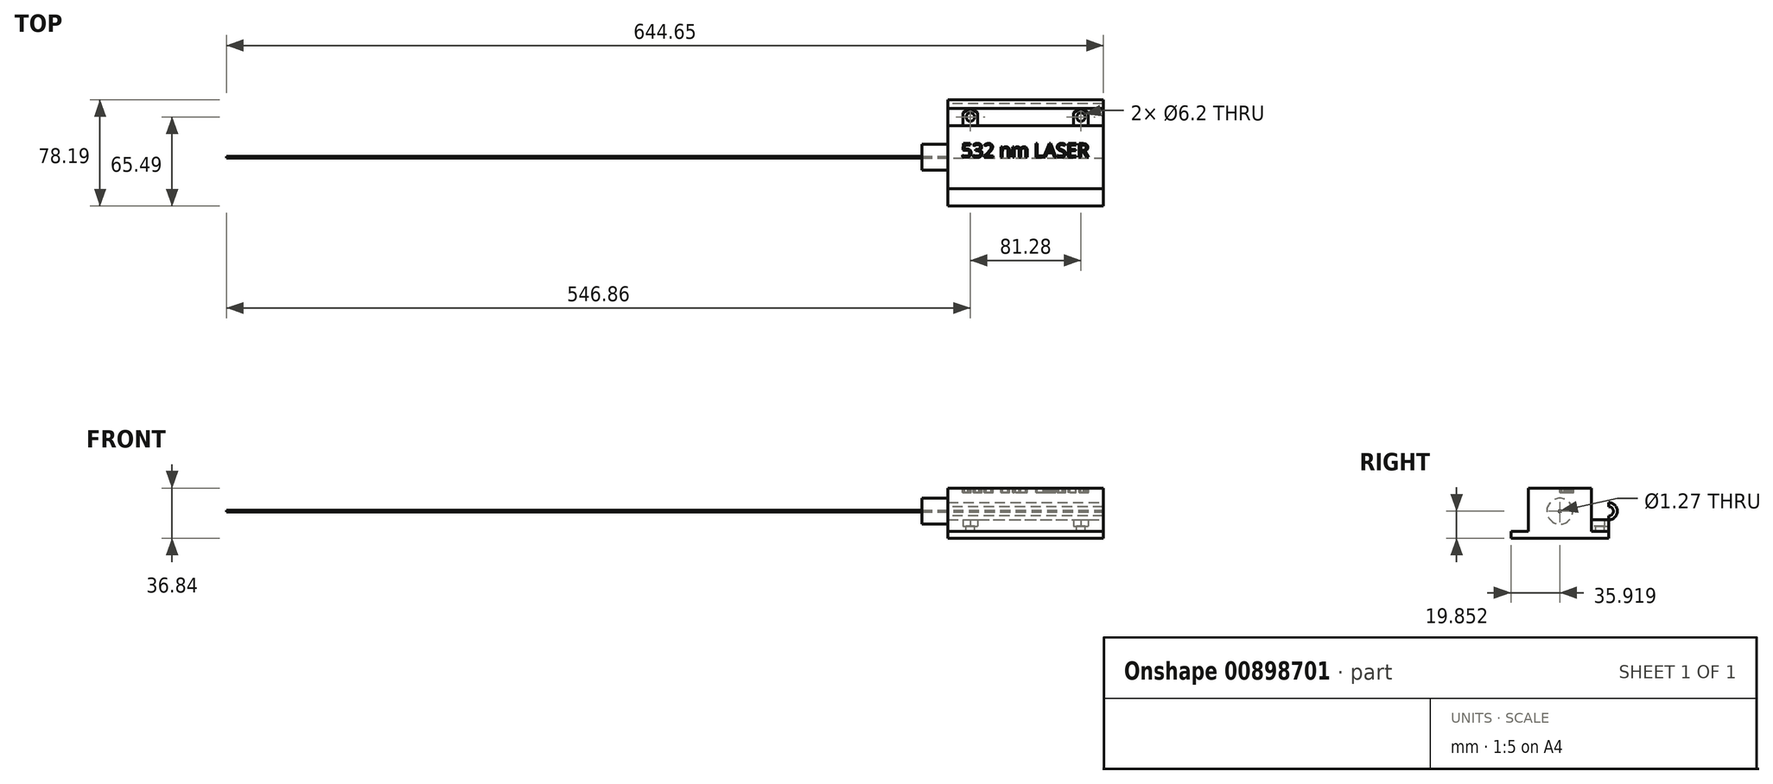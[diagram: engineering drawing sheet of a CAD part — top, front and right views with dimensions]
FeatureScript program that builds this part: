
annotation { "Feature Type Name" : "Feature", "Feature Type Description" : "" }
export const myFeature = defineFeature(function(context is Context, id is Id, definition is map)
    precondition{}
    {
        {
            var Q0;
            Q0=qCreatedBy(makeId("Top.planeOp"),FACE);
            var sketch = newSketch(context, id + "F0", { "sketchPlane" : qUnion([Q0])});
            skLineSegment(sketch, "E0.bottom", {"start": v(-57.15, 6.35) * mm, "end": v(57.15, 6.35) * mm});
            skLineSegment(sketch, "E0.top", {"start": v(-57.15, -6.35) * mm, "end": v(57.15, -6.35) * mm});
            skLineSegment(sketch, "E0.left", {"start": v(-57.15, 6.35) * mm, "end": v(-57.15, -6.35) * mm});
            skLineSegment(sketch, "E0.right", {"start": v(57.15, 6.35) * mm, "end": v(57.15, -6.35) * mm});
            skLineSegment(sketch, "E1", {"start": v(-57.15, 0) * mm, "end": v(57.15, 0) * mm, "construction": true});
            skLineSegment(sketch, "E2", {"start": v(0, -6.35) * mm, "end": v(0, 6.35) * mm, "construction": true});
            skSolve(sketch);
        }
        {
            var Q0;
            Q0=makeQuery(id+"F0.imprint","IMPRINT",FACE,{"disambiguationData":[TD([[makeQuery(id+"F0.imprint","IMPRINT",EDGE,{"derivedFrom":sQuery(id+"F0.wireOp",EDGE,"E0.bottom")}),-1.0]])]});
            extrude(context, id + "F1", {"entities" : qUnion([Q0]), "depth" : 3.8 * mm, "offsetDistance" : 25.4 * mm});
        }
        {
            var Q0;
            Q0=makeQuery(id+"F1.opExtrude","CAP_FACE",FACE,{"disambiguationData":[OSD([sQuery(id+"F0.wireOp",EDGE,"E0.bottom"),sQuery(id+"F0.wireOp",EDGE,"E0.top"),sQuery(id+"F0.wireOp",EDGE,"E0.left"),sQuery(id+"F0.wireOp",EDGE,"E0.right")])],"isStart":false});
            var sketch = newSketch(context, id + "F2", { "sketchPlane" : qUnion([Q0])});
            skLineSegment(sketch, "E3", {"start": v(-40.64, 0) * mm, "end": v(40.64, 0) * mm, "construction": true});
            skCircle(sketch, "E4", {"center": v(-40.64, 0) * mm, "radius": 3.1 * mm});
            skCircle(sketch, "E5", {"center": v(40.64, 0) * mm, "radius": 3.1 * mm});
            skCircle(sketch, "E6.cCircle", {"center": v(-40.64, 0) * mm, "radius": 5.46 * mm, "construction": true});
            skLineSegment(sketch, "E6.0", {"start": v(-35.18, 3.15) * mm, "end": v(-35.18, -3.15) * mm});
            skLineSegment(sketch, "E6.1", {"start": v(-35.18, -3.15) * mm, "end": v(-40.64, -6.3) * mm});
            skLineSegment(sketch, "E6.2", {"start": v(-40.64, -6.3) * mm, "end": v(-46.1, -3.15) * mm});
            skLineSegment(sketch, "E6.3", {"start": v(-46.1, -3.15) * mm, "end": v(-46.1, 3.15) * mm});
            skLineSegment(sketch, "E6.4", {"start": v(-46.1, 3.15) * mm, "end": v(-40.64, 6.3) * mm});
            skLineSegment(sketch, "E6.5", {"start": v(-40.64, 6.3) * mm, "end": v(-35.18, 3.15) * mm});
            skPoint(sketch, "E6.0.midPoint", {"position": v(-35.18, 0) * mm});
            skCircle(sketch, "E7.cCircle", {"center": v(40.64, 0) * mm, "radius": 5.46 * mm, "construction": true});
            skLineSegment(sketch, "E7.0", {"start": v(35.18, -3.15) * mm, "end": v(35.18, 3.15) * mm});
            skLineSegment(sketch, "E7.1", {"start": v(35.18, 3.15) * mm, "end": v(40.64, 6.3) * mm});
            skLineSegment(sketch, "E7.2", {"start": v(40.64, 6.3) * mm, "end": v(46.1, 3.15) * mm});
            skLineSegment(sketch, "E7.3", {"start": v(46.1, 3.15) * mm, "end": v(46.1, -3.15) * mm});
            skLineSegment(sketch, "E7.4", {"start": v(46.1, -3.15) * mm, "end": v(40.64, -6.3) * mm});
            skLineSegment(sketch, "E7.5", {"start": v(40.64, -6.3) * mm, "end": v(35.18, -3.15) * mm});
            skPoint(sketch, "E7.0.midPoint", {"position": v(35.18, 0) * mm});
            skLineSegment(sketch, "E8", {"start": v(-46.1, -3.15) * mm, "end": v(-46.1, -6.35) * mm});
            skLineSegment(sketch, "E9", {"start": v(-35.18, -3.15) * mm, "end": v(-35.18, -6.35) * mm});
            skLineSegment(sketch, "E10", {"start": v(35.18, -3.15) * mm, "end": v(35.18, -6.35) * mm});
            skLineSegment(sketch, "E11", {"start": v(46.1, -3.15) * mm, "end": v(46.1, -6.35) * mm});
            skSolve(sketch);
        }
        {
            var Q0;
            Q0=makeQuery(id+"F2.imprint","IMPRINT",FACE,{"disambiguationData":[TD([[makeQuery(id+"F2.imprint","IMPRINT",EDGE,{"derivedFrom":sQuery(id+"F2.wireOp",EDGE,"E6.0")}),1.0]])]});
            extrude(context, id + "F3", {"entities" : qUnion([Q0]), "operationType" : NewBodyOperationType.ADD, "depth" : 4.57 * mm, "offsetDistance" : 25.4 * mm});
        }
        {
            var Q0;
            Q0=makeQuery(id+"F3.opExtrude","CAP_FACE",FACE,{"disambiguationData":[OSD([sQuery(id+"F0.wireOp",EDGE,"E0.bottom"),sQuery(id+"F0.wireOp",EDGE,"E0.top"),sQuery(id+"F0.wireOp",EDGE,"E0.left"),sQuery(id+"F0.wireOp",EDGE,"E0.right"),sQuery(id+"F2.wireOp",EDGE,"E6.0"),sQuery(id+"F2.wireOp",EDGE,"E6.3"),sQuery(id+"F2.wireOp",EDGE,"E6.4"),sQuery(id+"F2.wireOp",EDGE,"E6.5"),sQuery(id+"F2.wireOp",EDGE,"E7.0"),sQuery(id+"F2.wireOp",EDGE,"E7.1"),sQuery(id+"F2.wireOp",EDGE,"E7.2"),sQuery(id+"F2.wireOp",EDGE,"E7.3"),sQuery(id+"F2.wireOp",EDGE,"E8"),sQuery(id+"F2.wireOp",EDGE,"E9"),sQuery(id+"F2.wireOp",EDGE,"E10"),sQuery(id+"F2.wireOp",EDGE,"E11")])],"isStart":false});
            var sketch = newSketch(context, id + "F4", { "sketchPlane" : qUnion([Q0])});
            skLineSegment(sketch, "E12.0", {"start": v(-57.15, -6.35) * mm, "end": v(57.15, -6.35) * mm});
            skLineSegment(sketch, "E12.1", {"start": v(-57.15, 6.35) * mm, "end": v(-57.15, -6.35) * mm});
            skLineSegment(sketch, "E12.2", {"start": v(-57.15, 6.35) * mm, "end": v(57.15, 6.35) * mm, "construction": true});
            skLineSegment(sketch, "E12.3", {"start": v(57.15, 6.35) * mm, "end": v(57.15, -6.35) * mm});
            skLineSegment(sketch, "E12.4", {"start": v(35.18, 3.15) * mm, "end": v(35.18, -6.35) * mm});
            skLineSegment(sketch, "E12.5", {"start": v(35.18, 3.15) * mm, "end": v(40.64, 6.3) * mm});
            skLineSegment(sketch, "E12.6", {"start": v(40.64, 6.3) * mm, "end": v(46.1, 3.15) * mm});
            skLineSegment(sketch, "E12.7", {"start": v(46.1, 3.15) * mm, "end": v(46.1, -6.35) * mm});
            skPoint(sketch, "E12.8", {"position": v(40.64, 0) * mm});
            skLineSegment(sketch, "E12.9", {"start": v(-46.1, 3.15) * mm, "end": v(-46.1, -6.35) * mm});
            skLineSegment(sketch, "E12.10", {"start": v(-46.1, 3.15) * mm, "end": v(-40.64, 6.3) * mm});
            skLineSegment(sketch, "E12.11", {"start": v(-40.64, 6.3) * mm, "end": v(-35.18, 3.15) * mm});
            skLineSegment(sketch, "E12.12", {"start": v(-35.18, 3.15) * mm, "end": v(-35.18, -6.35) * mm});
            skPoint(sketch, "E13.0", {"position": v(-40.64, 0) * mm});
            skLineSegment(sketch, "E14", {"start": v(-57.15, 6.35) * mm, "end": v(-57.15, 12.7) * mm});
            skLineSegment(sketch, "E15", {"start": v(57.15, 6.35) * mm, "end": v(57.15, 12.7) * mm});
            skLineSegment(sketch, "E16", {"start": v(-57.15, 12.7) * mm, "end": v(57.15, 12.7) * mm});
            skSolve(sketch);
        }
        {
            var Q0;
            Q0=makeQuery(id+"F4.imprint","IMPRINT",FACE,{"disambiguationData":[TD([[makeQuery(id+"F4.imprint","IMPRINT",EDGE,{"derivedFrom":sQuery(id+"F4.wireOp",EDGE,"E14")}),-1.0]])]});
            var Q1;
            {var subQ4=sQuery(id+"F4.wireOp",EDGE,"E12.1");Q1=makeQuery(id+"F4.imprint","IMPRINT",FACE,{"disambiguationData":[TD([[makeQuery(id+"F4.imprint","IMPRINT",EDGE,{"derivedFrom":subQ4}),1.0]])]});}
            extrude(context, id + "F5", {"entities" : qUnion([Q0, Q1]), "operationType" : NewBodyOperationType.ADD, "depth" : 1.02 * mm, "offsetDistance" : 25.4 * mm});
        }
        {
            var Q0;
            Q0=makeQuery(id+"F5.opExtrude","CAP_FACE",FACE,{"disambiguationData":[OSD([sQuery(id+"F4.wireOp",EDGE,"E12.0"),sQuery(id+"F4.wireOp",EDGE,"E12.1"),sQuery(id+"F4.wireOp",EDGE,"E12.3"),sQuery(id+"F4.wireOp",EDGE,"E12.4"),sQuery(id+"F4.wireOp",EDGE,"E12.5"),sQuery(id+"F4.wireOp",EDGE,"E12.6"),sQuery(id+"F4.wireOp",EDGE,"E12.7"),sQuery(id+"F4.wireOp",EDGE,"E12.9"),sQuery(id+"F4.wireOp",EDGE,"E12.10"),sQuery(id+"F4.wireOp",EDGE,"E12.11"),sQuery(id+"F4.wireOp",EDGE,"E12.12"),sQuery(id+"F4.wireOp",EDGE,"E14"),sQuery(id+"F4.wireOp",EDGE,"E15"),sQuery(id+"F4.wireOp",EDGE,"E16")])],"isStart":false});
            var sketch = newSketch(context, id + "F6", { "sketchPlane" : qUnion([Q0])});
            skLineSegment(sketch, "E17.0", {"start": v(-57.15, 12.7) * mm, "end": v(57.15, 12.7) * mm});
            skLineSegment(sketch, "E18.0", {"start": v(-57.15, -6.35) * mm, "end": v(-57.15, 12.7) * mm});
            skLineSegment(sketch, "E19.0", {"start": v(-57.15, -6.35) * mm, "end": v(57.15, -6.35) * mm});
            skLineSegment(sketch, "E20.0", {"start": v(57.15, -6.35) * mm, "end": v(57.15, 12.7) * mm});
            skSolve(sketch);
        }
        {
            var Q0;
            Q0=makeQuery(id+"F6.imprint","IMPRINT",FACE,{"disambiguationData":[TD([[makeQuery(id+"F6.imprint","IMPRINT",EDGE,{"derivedFrom":sQuery(id+"F6.wireOp",EDGE,"E17.0")}),-1.0]])]});
            var Q1;
            {var subQ0=makeQuery(id+"F5.opExtrude","CAP_EDGE",EDGE,{"disambiguationData":[OSD([sQuery(id+"F4.wireOp",EDGE,"E12.4")])],"isStart":false});Q1=makeQuery(id+"F6.imprint","IMPRINT",FACE,{"disambiguationData":[TD([[makeQuery(id+"F6.imprint","IMPRINT",EDGE,{"derivedFrom":subQ0}),1.0]])]});}
            var Q2;
            {var subQ1=makeQuery(id+"F5.opExtrude","CAP_EDGE",EDGE,{"disambiguationData":[OSD([sQuery(id+"F4.wireOp",EDGE,"E12.9")])],"isStart":false});Q2=makeQuery(id+"F6.imprint","IMPRINT",FACE,{"disambiguationData":[TD([[makeQuery(id+"F6.imprint","IMPRINT",EDGE,{"derivedFrom":subQ1}),1.0]])]});}
            extrude(context, id + "F7", {"entities" : qUnion([Q0, Q1, Q2]), "operationType" : NewBodyOperationType.ADD, "depth" : 11.68 * mm, "offsetDistance" : 25.4 * mm});
        }
        {
            var Q0;
            Q0=makeQuery(id+"F7.opExtrude","CAP_EDGE",EDGE,{"disambiguationData":[OSD([sQuery(id+"F6.wireOp",EDGE,"E17.0")])],"isStart":false});
            var Q1;
            Q1=makeQuery(id+"F7.opExtrude","CAP_EDGE",EDGE,{"disambiguationData":[OSD([sQuery(id+"F6.wireOp",EDGE,"E19.0")])],"isStart":false});
            var Q2;
            Q2=makeQuery(id+"F5.opExtrude","CAP_EDGE",EDGE,{"disambiguationData":[OSD([sQuery(id+"F4.wireOp",EDGE,"E16")])],"isStart":true});
            fillet(context, id + "F8", {"entities" : qUnion([Q0, Q1, Q2]), "radius" : 6.35 * mm, "tangentPropagation" : true, "allowEdgeOverflow" : false});
        }
        {
            var Q0;
            {var subQ0=sQuery(id+"F0.wireOp",EDGE,"E0.left");Q0=makeQuery(id+"F7.boolean.opBoolean","MERGE",FACE,{"derivedFrom":[makeQuery(id+"F5.boolean.opBoolean","MERGE",FACE,{"derivedFrom":[makeQuery(id+"F3.boolean.opBoolean","MERGE",FACE,{"derivedFrom":[makeQuery(id+"F1.opExtrude","SWEPT_FACE",FACE,{"disambiguationData":[OSD([subQ0])]}),makeQuery(id+"F3.opExtrude","SWEPT_FACE",FACE,{"disambiguationData":[OSD([subQ0])]})]}),makeQuery(id+"F5.opExtrude","SWEPT_FACE",FACE,{"disambiguationData":[OSD([sQuery(id+"F4.wireOp",EDGE,"E12.1"),sQuery(id+"F4.wireOp",EDGE,"E14")])]})]}),makeQuery(id+"F7.opExtrude","SWEPT_FACE",FACE,{"disambiguationData":[OSD([sQuery(id+"F6.wireOp",EDGE,"E18.0")])]})]});}
            var sketch = newSketch(context, id + "F9", { "sketchPlane" : qUnion([Q0])});
            skArc(sketch, "E21.0", {"start": v(-6.35, 21.08) * mm, "mid": v(-12.7, 14.73) * mm, "end": v(-6.35, 8.38) * mm, "construction": true});
            skCircle(sketch, "E22", {"center": v(-6.35, 14.73) * mm, "radius": 3.43 * mm});
            skLineSegment(sketch, "E23", {"start": v(-6.35, 14.73) * mm, "end": v(65.5, 14.73) * mm, "construction": true});
            skArc(sketch, "E24.0", {"start": v(6.35, 14.73) * mm, "mid": v(4.5, 19.22) * mm, "end": v(0, 21.08) * mm, "construction": true});
            skLineSegment(sketch, "E25.0", {"start": v(0, 21.08) * mm, "end": v(-6.35, 21.08) * mm, "construction": true});
            skLineSegment(sketch, "E26.0", {"start": v(-6.35, 8.38) * mm, "end": v(-6.35, 0) * mm, "construction": true});
            skLineSegment(sketch, "E27.0", {"start": v(-6.35, 0) * mm, "end": v(6.35, 0) * mm, "construction": true});
            skLineSegment(sketch, "E28.0", {"start": v(6.35, 14.73) * mm, "end": v(6.35, 0) * mm, "construction": true});
            skLineSegment(sketch, "E29", {"start": v(29.57, 14.73) * mm, "end": v(29.57, 0) * mm, "construction": true});
            skArc(sketch, "E30.MirrorCS", {"start": v(65.5, 21.08) * mm, "mid": v(71.84, 14.73) * mm, "end": v(65.5, 8.38) * mm, "construction": true});
            skArc(sketch, "E31.MirrorCS", {"start": v(52.8, 14.73) * mm, "mid": v(54.65, 19.22) * mm, "end": v(59.14, 21.08) * mm, "construction": true});
            skLineSegment(sketch, "E32.MirrorCS", {"start": v(59.14, 21.08) * mm, "end": v(65.5, 21.08) * mm, "construction": true});
            skLineSegment(sketch, "E33.MirrorCS", {"start": v(65.5, 8.38) * mm, "end": v(65.5, 0) * mm, "construction": true});
            skLineSegment(sketch, "E34.MirrorCS", {"start": v(65.5, 0) * mm, "end": v(52.8, 0) * mm, "construction": true});
            skLineSegment(sketch, "E35.MirrorCS", {"start": v(52.8, 14.73) * mm, "end": v(52.8, 0) * mm, "construction": true});
            skLineSegment(sketch, "E36", {"start": v(-6.35, 0) * mm, "end": v(6.35, 0) * mm});
            skLineSegment(sketch, "E37", {"start": v(6.35, 31.72) * mm, "end": v(52.8, 31.72) * mm});
            skLineSegment(sketch, "E38", {"start": v(52.8, 31.72) * mm, "end": v(52.8, 0) * mm});
            skLineSegment(sketch, "E39", {"start": v(65.5, 0) * mm, "end": v(65.5, -5.12) * mm});
            skLineSegment(sketch, "E40", {"start": v(65.5, -5.12) * mm, "end": v(-6.35, -5.12) * mm});
            skLineSegment(sketch, "E41", {"start": v(-6.35, -5.12) * mm, "end": v(-6.35, 0) * mm});
            skLineSegment(sketch, "E42", {"start": v(6.35, 0) * mm, "end": v(6.35, 31.72) * mm});
            skLineSegment(sketch, "E43", {"start": v(52.8, 0) * mm, "end": v(65.5, 0) * mm});
            skCircle(sketch, "E44", {"center": v(29.57, 14.73) * mm, "radius": 9.53 * mm});
            skCircle(sketch, "E45", {"center": v(29.57, 14.73) * mm, "radius": 0.64 * mm});
            skSolve(sketch);
        }
        {
            var Q0;
            Q0=qSketchRegion(id+"F9",true);
            extrude(context, id + "F10", {"entities" : qUnion([Q0]), "operationType" : NewBodyOperationType.REMOVE, "endBound" : BoundingType.THROUGH_ALL, "oppositeDirection" : true, "depth" : 25.4 * mm, "offsetDistance" : 25.4 * mm});
        }
        {
            var Q0;
            Q0=makeQuery(id+"F2.imprint","IMPRINT",FACE,{"disambiguationData":[TD([[makeQuery(id+"F2.imprint","IMPRINT",EDGE,{"derivedFrom":sQuery(id+"F2.wireOp",EDGE,"E4")}),1.0]])]});
            var Q1;
            Q1=makeQuery(id+"F2.imprint","IMPRINT",FACE,{"disambiguationData":[TD([[makeQuery(id+"F2.imprint","IMPRINT",EDGE,{"derivedFrom":sQuery(id+"F2.wireOp",EDGE,"E5")}),1.0]])]});
            extrude(context, id + "F11", {"entities" : qUnion([Q0, Q1]), "operationType" : NewBodyOperationType.REMOVE, "oppositeDirection" : true, "depth" : 21.34 * mm, "offsetDistance" : 25.4 * mm, "symmetric" : true});
        }
        {
            var Q0;
            {var subQ1=sQuery(id+"F9.wireOp",EDGE,"E36");Q0=makeQuery(id+"F9.imprint","IMPRINT",FACE,{"disambiguationData":[TD([[makeQuery(id+"F9.imprint","IMPRINT",EDGE,{"derivedFrom":subQ1}),-1.0]])]});}
            extrude(context, id + "F12", {"entities" : qUnion([Q0]), "oppositeDirection" : true, "depth" : 114.3 * mm, "offsetDistance" : 25.4 * mm});
        }
        {
            var Q0;
            Q0=makeQuery(id+"F9.imprint","IMPRINT",FACE,{"disambiguationData":[TD([[makeQuery(id+"F9.imprint","IMPRINT",EDGE,{"derivedFrom":sQuery(id+"F9.wireOp",EDGE,"E44")}),1.0]])]});
            extrude(context, id + "F13", {"entities" : qUnion([Q0]), "operationType" : NewBodyOperationType.ADD, "depth" : 38.1 * mm, "offsetDistance" : 25.4 * mm, "symmetric" : true});
        }
        {
            var Q0;
            Q0=makeQuery(id+"F12.opExtrude","SWEPT_FACE",FACE,{"disambiguationData":[OSD([sQuery(id+"F9.wireOp",EDGE,"E37")])]});
            var sketch = newSketch(context, id + "F14", { "sketchPlane" : qUnion([Q0])});
            skText(sketch, "E46", { "text": "532 nm LASER", "fontName": "OpenSans-Regular.ttf"});
            skPoint(sketch, "E46.secondSnap0", {"position": v(57.15, -29.57) * mm});
            skLineSegment(sketch, "E47", {"start": v(0, 0) * mm, "end": v(0, -52.8) * mm, "construction": true});
            skLineSegment(sketch, "E48", {"start": v(-57.15, -29.57) * mm, "end": v(57.15, -29.57) * mm});
            skPoint(sketch, "E49", {"position": v(0, -29.57) * mm});
            const initialGuessF14  = {"E46": [-0.04728, -0.02957, 1, 0, 0.01016]};
            skSetInitialGuess(sketch, initialGuessF14);
            skSolve(sketch);
        }
        {
            var Q0;
            Q0=makeQuery(id+"F14.imprint","IMPRINT",FACE,{"disambiguationData":[TD([[makeQuery(id+"F14.imprint","IMPRINT",EDGE,{"derivedFrom":sQuery(id+"F14.wireOp",EDGE,"E46.sketch_text.stroke-0")}),-1.0]])]});
            var Q1;
            Q1=makeQuery(id+"F14.imprint","IMPRINT",FACE,{"disambiguationData":[TD([[makeQuery(id+"F14.imprint","IMPRINT",EDGE,{"derivedFrom":sQuery(id+"F14.wireOp",EDGE,"E46.sketch_text.stroke-19")}),-1.0]])]});
            var Q2;
            {var subQ0=sQuery(id+"F14.wireOp",EDGE,"E46.sketch_text.stroke-48");Q2=makeQuery(id+"F14.imprint","IMPRINT",FACE,{"disambiguationData":[TD([[makeQuery(id+"F14.imprint","IMPRINT",EDGE,{"derivedFrom":subQ0}),-1.0]])]});}
            var Q3;
            {var subQ3=sQuery(id+"F14.wireOp",EDGE,"E46.sketch_text.stroke-67");Q3=makeQuery(id+"F14.imprint","IMPRINT",FACE,{"disambiguationData":[TD([[makeQuery(id+"F14.imprint","IMPRINT",EDGE,{"derivedFrom":subQ3}),-1.0]])]});}
            var Q4;
            {var subQ1=sQuery(id+"F14.wireOp",EDGE,"E46.sketch_text.stroke-84");Q4=makeQuery(id+"F14.imprint","IMPRINT",FACE,{"disambiguationData":[TD([[makeQuery(id+"F14.imprint","IMPRINT",EDGE,{"derivedFrom":subQ1}),-1.0]])]});}
            var Q5;
            {var subQ0=sQuery(id+"F14.wireOp",EDGE,"E46.sketch_text.stroke-112");Q5=makeQuery(id+"F14.imprint","IMPRINT",FACE,{"disambiguationData":[TD([[makeQuery(id+"F14.imprint","IMPRINT",EDGE,{"derivedFrom":subQ0}),-1.0]])]});}
            var Q6;
            {var subQ1=sQuery(id+"F14.wireOp",EDGE,"E46.sketch_text.stroke-118");Q6=makeQuery(id+"F14.imprint","IMPRINT",FACE,{"disambiguationData":[TD([[makeQuery(id+"F14.imprint","IMPRINT",EDGE,{"derivedFrom":subQ1}),-1.0]])]});}
            var Q7;
            {var subQ5=sQuery(id+"F14.wireOp",EDGE,"E46.sketch_text.stroke-131");Q7=makeQuery(id+"F14.imprint","IMPRINT",FACE,{"disambiguationData":[TD([[makeQuery(id+"F14.imprint","IMPRINT",EDGE,{"derivedFrom":subQ5}),-1.0]])]});}
            var Q8;
            {var subQ1=sQuery(id+"F14.wireOp",EDGE,"E46.sketch_text.stroke-157");Q8=makeQuery(id+"F14.imprint","IMPRINT",FACE,{"disambiguationData":[TD([[makeQuery(id+"F14.imprint","IMPRINT",EDGE,{"derivedFrom":subQ1}),-1.0]])]});}
            var Q9;
            {var subQ2=sQuery(id+"F14.wireOp",EDGE,"E46.sketch_text.stroke-168");Q9=makeQuery(id+"F14.imprint","IMPRINT",FACE,{"disambiguationData":[TD([[makeQuery(id+"F14.imprint","IMPRINT",EDGE,{"derivedFrom":subQ2}),-1.0]])]});}
            extrude(context, id + "F15", {"entities" : qUnion([Q0, Q1, Q2, Q3, Q4, Q5, Q6, Q7, Q8, Q9]), "operationType" : NewBodyOperationType.REMOVE, "oppositeDirection" : true, "depth" : 3.17 * mm, "offsetDistance" : 25.4 * mm});
        }
        {
            var Q0;
            Q0=makeQuery(id+"F9.imprint","IMPRINT",FACE,{"disambiguationData":[TD([[makeQuery(id+"F9.imprint","IMPRINT",EDGE,{"derivedFrom":sQuery(id+"F9.wireOp",EDGE,"E44")}),1.0]])]});
            extrude(context, id + "F16", {"entities" : qUnion([Q0]), "operationType" : NewBodyOperationType.ADD, "oppositeDirection" : true, "depth" : 114.3 * mm, "offsetDistance" : 25.4 * mm});
        }
        {
            var Q0;
            Q0=makeQuery(id+"F9.imprint","IMPRINT",FACE,{"disambiguationData":[TD([[makeQuery(id+"F9.imprint","IMPRINT",EDGE,{"derivedFrom":sQuery(id+"F9.wireOp",EDGE,"E45")}),1.0]])]});
            extrude(context, id + "F17", {"entities" : qUnion([Q0]), "depth" : 530.35 * mm, "offsetDistance" : 25.4 * mm});
        }
    });
